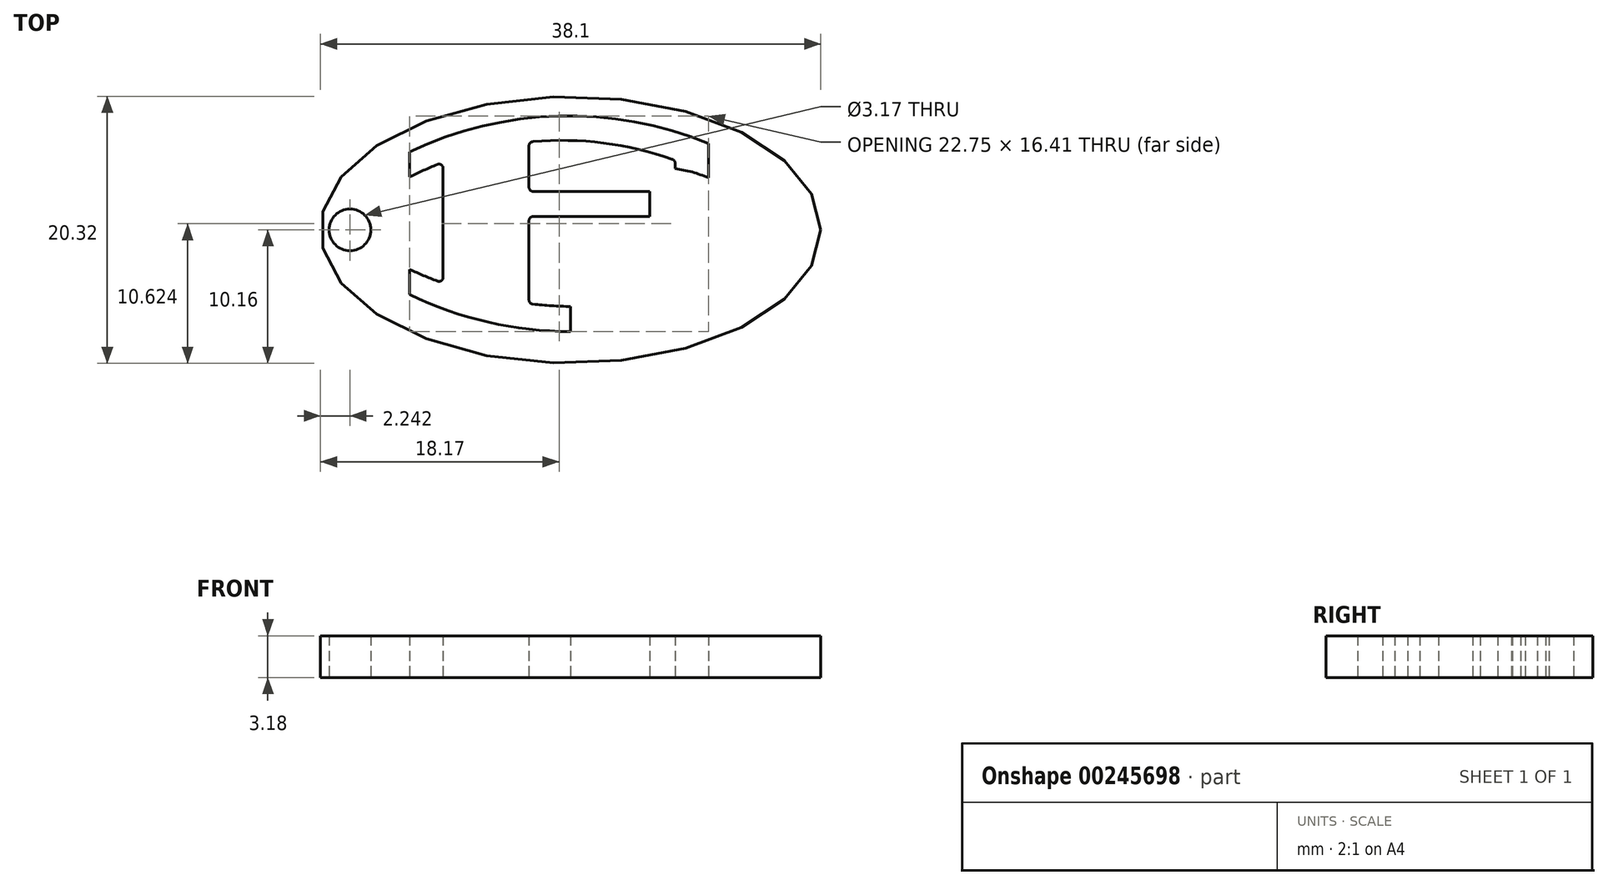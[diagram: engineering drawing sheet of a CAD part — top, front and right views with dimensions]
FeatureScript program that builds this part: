
annotation { "Feature Type Name" : "Feature", "Feature Type Description" : "" }
export const myFeature = defineFeature(function(context is Context, id is Id, definition is map)
    precondition{}
    {
        {
            var Q0;
            Q0=qCreatedBy(makeId("Top.planeOp"),FACE);
            var sketch = newSketch(context, id + "F0", { "sketchPlane" : qUnion([Q0])});
            skEllipse(sketch, "E0", {"center": v(0, 0) * mm, "majorRadius": 19.05 * mm, "minorRadius": 10.16 * mm, "majorAxis": v(1, 0)});
            skArc(sketch, "E1", {"start": v(10.5, 6.57) * mm, "mid": v(-0.95, 8.67) * mm, "end": v(-12.25, 5.93) * mm});
            skLineSegment(sketch, "E2", {"start": v(-12.25, 5.93) * mm, "end": v(-12.25, 4.02) * mm});
            skArc(sketch, "E3", {"start": v(-12.25, -4.92) * mm, "mid": v(-6.29, -7.03) * mm, "end": v(0, -7.74) * mm});
            skLineSegment(sketch, "E4", {"start": v(10.5, 6.57) * mm, "end": v(10.5, 3.98) * mm});
            skLineSegment(sketch, "E5", {"start": v(7.95, 4.67) * mm, "end": v(7.95, 5.08) * mm});
            skArc(sketch, "E6", {"start": v(7.74, 5.38) * mm, "mid": v(2.5, 6.62) * mm, "end": v(-2.89, 6.72) * mm});
            skLineSegment(sketch, "E7", {"start": v(-12.25, -4.92) * mm, "end": v(-12.25, -3.01) * mm});
            skLineSegment(sketch, "E8", {"start": v(0, -7.74) * mm, "end": v(0, -5.84) * mm});
            skArc(sketch, "E9", {"start": v(-12.25, -3.01) * mm, "mid": v(-11.2, -3.48) * mm, "end": v(-10.14, -3.9) * mm});
            skLineSegment(sketch, "E10", {"start": v(-9.71, -3.6) * mm, "end": v(-9.71, 4.69) * mm});
            skArc(sketch, "E11.trimOffspring", {"start": v(-2.9, -5.65) * mm, "mid": v(-1.45, -5.78) * mm, "end": v(0, -5.84) * mm});
            skArc(sketch, "E12.trimOffspring", {"start": v(-10.15, 4.98) * mm, "mid": v(-11.21, 4.53) * mm, "end": v(-12.25, 4.02) * mm});
            skLineSegment(sketch, "E13", {"start": v(-2.86, 2.93) * mm, "end": v(6.03, 2.93) * mm});
            skLineSegment(sketch, "E14", {"start": v(6.03, 2.93) * mm, "end": v(6.03, 1.02) * mm});
            skLineSegment(sketch, "E15", {"start": v(-3.18, -5.34) * mm, "end": v(-3.18, 0.7) * mm});
            skLineSegment(sketch, "E16.trimOffspring", {"start": v(-3.18, 3.24) * mm, "end": v(-3.18, 6.4) * mm});
            skArc(sketch, "E17", {"start": v(10.5, 3.98) * mm, "mid": v(9.24, 4.4) * mm, "end": v(7.95, 4.67) * mm});
            skPoint(sketch, "E18.visualSharp", {"position": v(-3.18, 6.7) * mm});
            skArc(sketch, "E18.filletArc", {"start": v(-2.89, 6.72) * mm, "mid": v(-3.1, 6.62) * mm, "end": v(-3.18, 6.4) * mm});
            skPoint(sketch, "E19.visualSharp", {"position": v(-3.18, 2.93) * mm});
            skArc(sketch, "E19.filletArc", {"start": v(-3.18, 3.24) * mm, "mid": v(-3.08, 3.02) * mm, "end": v(-2.86, 2.93) * mm});
            skPoint(sketch, "E20.visualSharp", {"position": v(-3.18, -5.62) * mm});
            skArc(sketch, "E20.filletArc", {"start": v(-3.18, -5.34) * mm, "mid": v(-3.1, -5.55) * mm, "end": v(-2.9, -5.65) * mm});
            skPoint(sketch, "E21.visualSharp", {"position": v(-9.71, -4.06) * mm});
            skArc(sketch, "E21.filletArc", {"start": v(-10.14, -3.9) * mm, "mid": v(-9.85, -3.87) * mm, "end": v(-9.71, -3.6) * mm});
            skPoint(sketch, "E22.visualSharp", {"position": v(-9.71, 5.15) * mm});
            skArc(sketch, "E22.filletArc", {"start": v(-9.71, 4.69) * mm, "mid": v(-9.85, 4.95) * mm, "end": v(-10.15, 4.98) * mm});
            skPoint(sketch, "E23.visualSharp", {"position": v(7.95, 5.3) * mm});
            skArc(sketch, "E23.filletArc", {"start": v(7.95, 5.08) * mm, "mid": v(7.9, 5.27) * mm, "end": v(7.74, 5.38) * mm});
            skCircle(sketch, "E24", {"center": v(-16.8, 0) * mm, "radius": 1.59 * mm});
            skLineSegment(sketch, "E25", {"start": v(6.03, 1.02) * mm, "end": v(-2.86, 1.02) * mm});
            skPoint(sketch, "E26.visualSharp", {"position": v(-3.18, 1.02) * mm});
            skArc(sketch, "E26.filletArc", {"start": v(-2.86, 1.02) * mm, "mid": v(-3.08, 0.93) * mm, "end": v(-3.18, 0.7) * mm});
            skSolve(sketch);
        }
        {
            var Q0;
            Q0=makeQuery(id+"F0.imprint","IMPRINT",FACE,{"disambiguationData":[TD([[makeQuery(id+"F0.imprint","IMPRINT",EDGE,{"derivedFrom":sQuery(id+"F0.wireOp",EDGE,"E0")}),1.0]])]});
            extrude(context, id + "F1", {"entities" : qUnion([Q0]), "depth" : 3.17 * mm});
        }
    });
